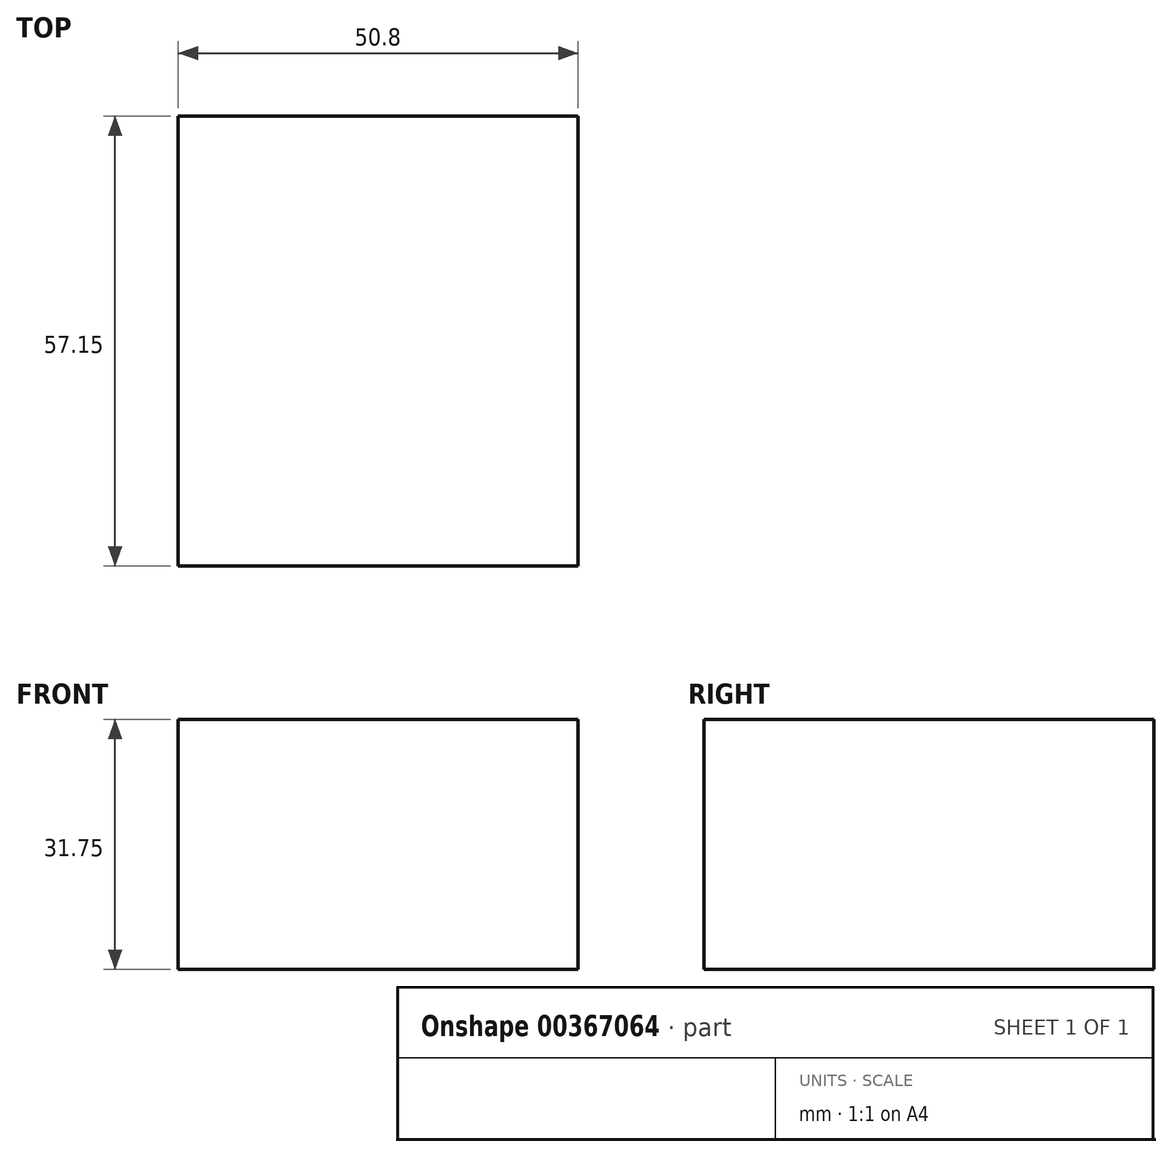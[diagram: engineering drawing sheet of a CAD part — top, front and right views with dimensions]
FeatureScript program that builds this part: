
annotation { "Feature Type Name" : "Feature", "Feature Type Description" : "" }
export const myFeature = defineFeature(function(context is Context, id is Id, definition is map)
    precondition{}
    {
        {
            var Q0;
            Q0=qCreatedBy(makeId("Front.planeOp"),FACE);
            var sketch = newSketch(context, id + "F0", { "sketchPlane" : qUnion([Q0])});
            skLineSegment(sketch, "E0", {"start": v(0, 0) * mm, "end": v(0, 31.75) * mm});
            skLineSegment(sketch, "E1", {"start": v(0, 31.75) * mm, "end": v(50.8, 31.75) * mm});
            skLineSegment(sketch, "E2", {"start": v(50.8, 31.75) * mm, "end": v(50.8, 0) * mm});
            skLineSegment(sketch, "E3", {"start": v(50.8, 0) * mm, "end": v(0, 0) * mm});
            skSolve(sketch);
        }
        {
            var Q0;
            Q0 = qSketchRegion(id + "F0", true);
            extrude(context, id + "F1", {"entities" : qUnion([Q0]), "depth" : 31.75 * mm});
        }
        {
            var Q0;
            Q0=makeQuery(id+"F1.opExtrude","CAP_FACE",FACE,{"disambiguationData":[OSD([sQuery(id+"F0.wireOp",EDGE,"E0"),sQuery(id+"F0.wireOp",EDGE,"E1"),sQuery(id+"F0.wireOp",EDGE,"E2"),sQuery(id+"F0.wireOp",EDGE,"E3")])],"isStart":false});
            extrude(context, id + "F2", {"entities" : qUnion([Q0]), "operationType" : NewBodyOperationType.ADD, "depth" : 25.4 * mm});
        }
    });
